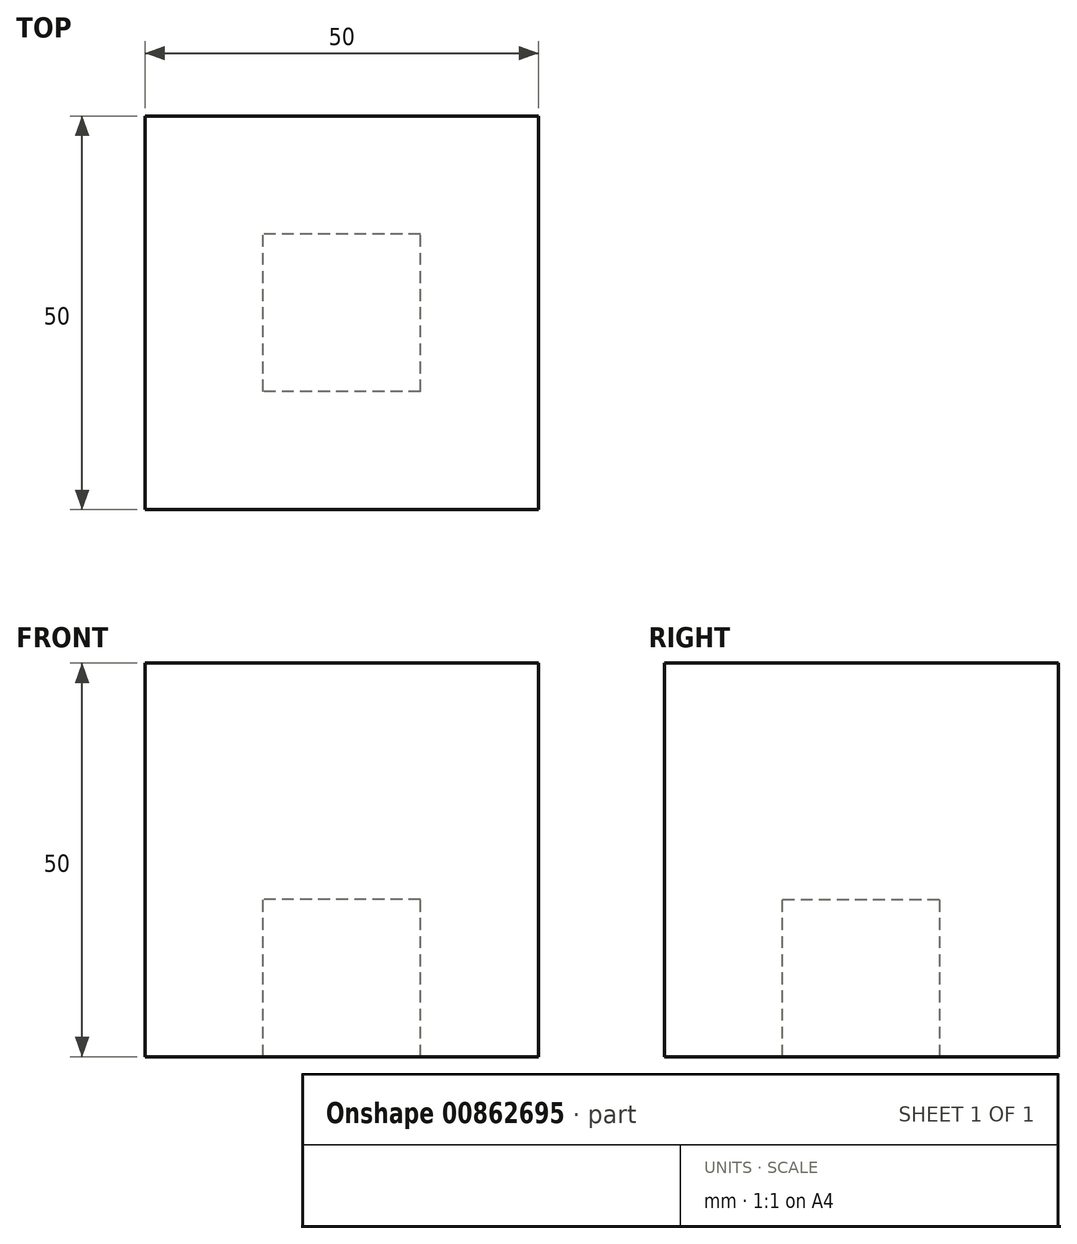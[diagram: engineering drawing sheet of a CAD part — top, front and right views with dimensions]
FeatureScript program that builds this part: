
annotation { "Feature Type Name" : "Feature", "Feature Type Description" : "" }
export const myFeature = defineFeature(function(context is Context, id is Id, definition is map)
    precondition{}
    {
        {
            var Q0;
            Q0=qCreatedBy(makeId("Front.planeOp"),FACE);
            var sketch = newSketch(context, id + "F0", { "sketchPlane" : qUnion([Q0])});
            skLineSegment(sketch, "E0.bottom", {"start": v(-25, -25) * mm, "end": v(25, -25) * mm});
            skLineSegment(sketch, "E0.top", {"start": v(-25, 25) * mm, "end": v(25, 25) * mm});
            skLineSegment(sketch, "E0.left", {"start": v(-25, -25) * mm, "end": v(-25, 25) * mm});
            skLineSegment(sketch, "E0.right", {"start": v(25, -25) * mm, "end": v(25, 25) * mm});
            skPoint(sketch, "E0.middle", {"position": v(0, 0) * mm});
            skLineSegment(sketch, "E1.bottom", {"start": v(-10, -25) * mm, "end": v(10, -25) * mm});
            skLineSegment(sketch, "E1.top", {"start": v(-10, -5) * mm, "end": v(10, -5) * mm});
            skLineSegment(sketch, "E1.left", {"start": v(-10, -25) * mm, "end": v(-10, -5) * mm});
            skLineSegment(sketch, "E1.right", {"start": v(10, -25) * mm, "end": v(10, -5) * mm});
            skPoint(sketch, "E1.middle", {"position": v(0, -15) * mm});
            skSolve(sketch);
        }
        {
            var Q0;
            Q0=makeQuery(id+"F0.imprint","IMPRINT",FACE,{"disambiguationData":[TD([[makeQuery(id+"F0.imprint","IMPRINT",EDGE,{"derivedFrom":sQuery(id+"F0.wireOp",EDGE,"E0.bottom")}),1.0]])]});
            extrude(context, id + "F1", {"entities" : qUnion([Q0]), "endBound" : BoundingType.SYMMETRIC, "depth" : 50 * mm, "offsetDistance" : 25 * mm});
        }
        {
            var Q0;
            Q0=qCreatedBy(makeId("Right.planeOp"),FACE);
            var sketch = newSketch(context, id + "F2", { "sketchPlane" : qUnion([Q0])});
            skLineSegment(sketch, "E2.bottom", {"start": v(25, 25) * mm, "end": v(-25, 25) * mm});
            skLineSegment(sketch, "E2.left", {"start": v(25, 25) * mm, "end": v(25, -25) * mm});
            skLineSegment(sketch, "E2.right", {"start": v(-25, 25) * mm, "end": v(-25, -25) * mm});
            skPoint(sketch, "E2.middle", {"position": v(0, 0) * mm});
            skLineSegment(sketch, "E3.top", {"start": v(10, -5) * mm, "end": v(-10, -5) * mm});
            skLineSegment(sketch, "E3.left", {"start": v(10, -25) * mm, "end": v(10, -5) * mm});
            skLineSegment(sketch, "E3.right", {"start": v(-10, -25) * mm, "end": v(-10, -5) * mm});
            skPoint(sketch, "E3.middle", {"position": v(0, -15) * mm});
            skLineSegment(sketch, "E4", {"start": v(-25, -25) * mm, "end": v(-10, -25) * mm});
            skLineSegment(sketch, "E5", {"start": v(10, -25) * mm, "end": v(25, -25) * mm});
            skSolve(sketch);
        }
        {
            var Q0;
            Q0 = qSketchRegion(id + "F2", true);
            extrude(context, id + "F3", {"entities" : qUnion([Q0]), "operationType" : NewBodyOperationType.ADD, "endBound" : BoundingType.SYMMETRIC, "depth" : 50 * mm, "offsetDistance" : 25 * mm});
        }
    });
